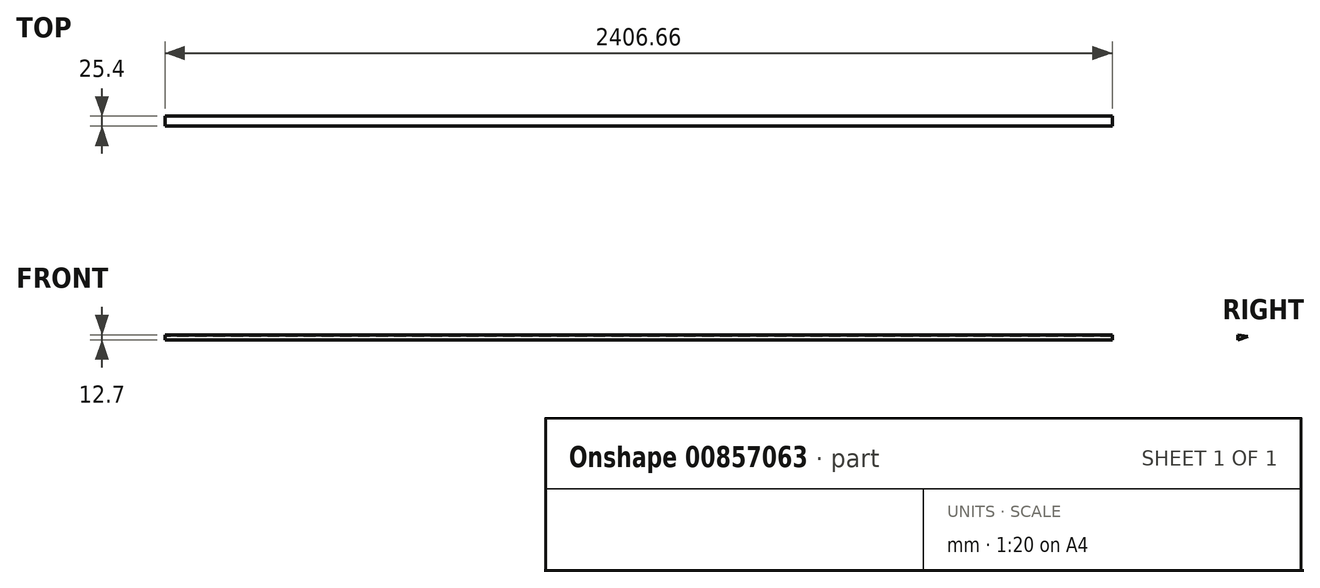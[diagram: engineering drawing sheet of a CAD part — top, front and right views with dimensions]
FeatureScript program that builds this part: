
annotation { "Feature Type Name" : "Feature", "Feature Type Description" : "" }
export const myFeature = defineFeature(function(context is Context, id is Id, definition is map)
    precondition{}
    {
        {
            var Q0;
            Q0=qCreatedBy(makeId("Right.planeOp"),FACE);
            var sketch = newSketch(context, id + "F0", { "sketchPlane" : qUnion([Q0])});
            skCircle(sketch, "E0", {"center": v(411.16, 74.61) * mm, "radius": 2.78 * mm});
            skLineSegment(sketch, "E1", {"start": v(101.2, 25.8) * mm, "end": v(411.57, 71.86) * mm});
            skPoint(sketch, "E2", {"position": v(76.2, 50.8) * mm});
            skCircle(sketch, "E3", {"center": v(76.2, 50.8) * mm, "radius": 76.2 * mm});
            skLineSegment(sketch, "E4", {"start": v(0, 50.8) * mm, "end": v(0, 0) * mm});
            skLineSegment(sketch, "E5", {"start": v(101.2, 25.8) * mm, "end": v(0, 13.16) * mm});
            skLineSegment(sketch, "E6", {"start": v(101.2, 25.8) * mm, "end": v(0, 10.78) * mm});
            skLineSegment(sketch, "E7", {"start": v(87.55, 126.15) * mm, "end": v(411.58, 77.36) * mm});
            skCircle(sketch, "E8", {"center": v(73.42, 50.8) * mm, "radius": 6.35 * mm});
            skLineSegment(sketch, "E9.bottom", {"start": v(101.2, 25.8) * mm, "end": v(104.38, 25.8) * mm});
            skLineSegment(sketch, "E9.top", {"start": v(101.2, 51.2) * mm, "end": v(104.38, 51.2) * mm});
            skLineSegment(sketch, "E9.left", {"start": v(101.2, 25.8) * mm, "end": v(101.2, 51.2) * mm});
            skLineSegment(sketch, "E9.right", {"start": v(104.38, 25.8) * mm, "end": v(104.38, 51.2) * mm});
            skPoint(sketch, "E10", {"position": v(104.38, 26.27) * mm});
            skLineSegment(sketch, "E11", {"start": v(113.06, 117.5) * mm, "end": v(357.95, 80.62) * mm});
            skLineSegment(sketch, "E12", {"start": v(145.37, 112.63) * mm, "end": v(145.37, 99.93) * mm});
            skLineSegment(sketch, "E13", {"start": v(145.37, 99.93) * mm, "end": v(170.77, 108.8) * mm});
            skLineSegment(sketch, "E14", {"start": v(145.37, 112.63) * mm, "end": v(145.37, 117.4) * mm});
            skSolve(sketch);
        }
        {
            var Q0;
            {var subQ0=sQuery(id+"F0.wireOp",EDGE,"E12");Q0=makeQuery(id+"F0.imprint","IMPRINT",FACE,{"disambiguationData":[TD([[makeQuery(id+"F0.imprint","IMPRINT",EDGE,{"derivedFrom":subQ0}),1.0]])]});}
            extrude(context, id + "F1", {"entities" : qUnion([Q0]), "depth" : 2406.65 * mm, "offsetDistance" : 25.4 * mm, "symmetric" : true});
        }
    });
